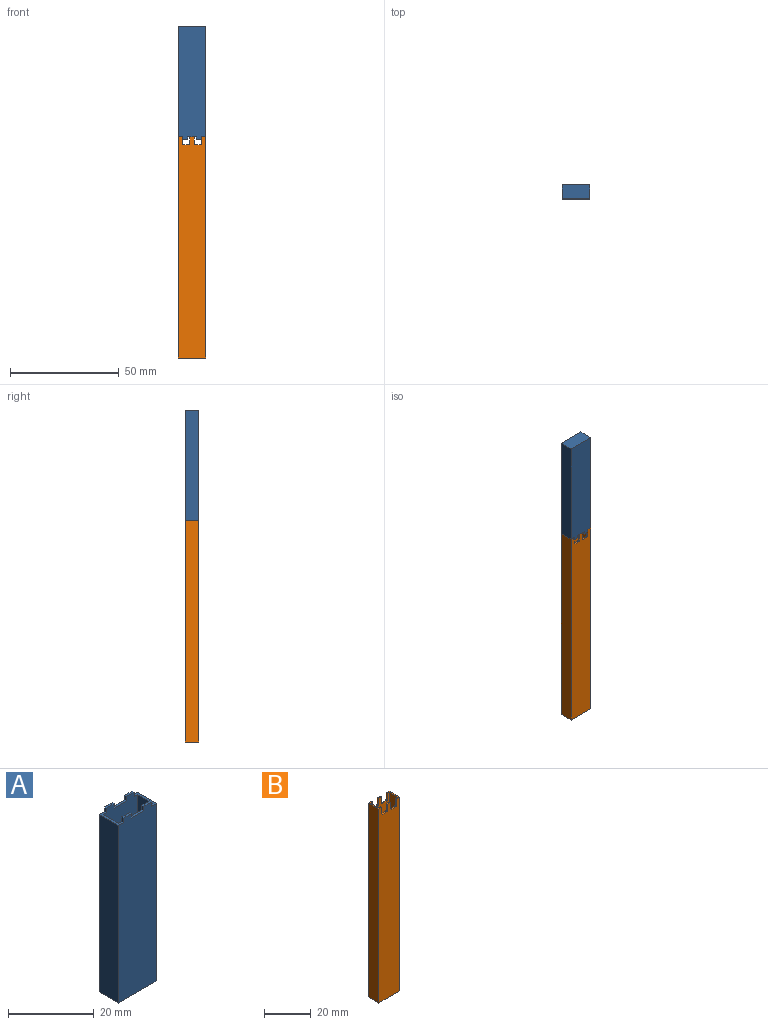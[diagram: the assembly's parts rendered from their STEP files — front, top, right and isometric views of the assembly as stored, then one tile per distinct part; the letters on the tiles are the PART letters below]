
ASSEMBLY  parts=2 mates=1
PART A: 26 faces, bbox 12.7x6.4x52.1 mm
  f0: plane 2.54x0.64mm, normal (0,0,1), area 1.6mm2, adj f9,f15,f20,f22
  f1: plane 2.54x0.64mm, normal (0,0,1), area 1.6mm2, adj f9,f15,f23,f24
  f2: plane 1.27x0.64mm, normal (1,0,0), area 0.8mm2, adj f7,f8,f13,f21
  f3: plane 1.27x0.64mm, normal (-1,0,0), area 0.8mm2, adj f8,f11,f13,f21
  f4: plane 1.27x0.64mm, normal (-1,0,0), area 0.8mm2, adj f7,f8,f13,f25
  f5: plane 1.27x0.64mm, normal (1,0,0), area 0.8mm2, adj f8,f10,f13,f25
  f6: plane 4.06x0.64mm, normal (0,0,1), area 2.6mm2, adj f9,f15,f20,f23
  f7: plane 4.06x0.64mm, normal (0,0,1), area 2.6mm2, adj f2,f4,f8,f13
  f8: plane 51.44x11.43mm, normal (0,-1,0), area 579.8mm2, adj f2,f3,f4,f5,f7,f10,f11,f17
  f9: plane 51.44x11.43mm, normal (0,1,0), area 579.8mm2, adj f0,f1,f6,f10,f11,f17,f18,f19
  f10: plane 6.35x1.78mm, normal (0,0,1), area 5.5mm2, adj f5,f8,f9,f12,f13,f15,f17,f24
  f11: plane 6.35x1.78mm, normal (0,0,1), area 5.5mm2, adj f3,f8,f9,f13,f14,f15,f18,f22
  f12: plane 50.8x6.35mm, normal (1,0,0), area 322.6mm2, adj f10,f13,f15,f16
  f13: plane 52.07x12.7mm, normal (0,1,0), area 651.6mm2, adj f2,f3,f4,f5,f7,f10,f11,f12
  f14: plane 50.8x6.35mm, normal (-1,0,0), area 322.6mm2, adj f11,f13,f15,f16
  f15: plane 52.07x12.7mm, normal (0,-1,0), area 651.6mm2, adj f0,f1,f6,f10,f11,f12,f14,f16
  f16: plane 12.7x6.35mm, normal (0,0,-1), area 80.6mm2, adj f12,f13,f14,f15
  f17: plane 50.17x5.08mm, normal (-1,0,0), area 254.8mm2, adj f8,f9,f10,f19
  f18: plane 50.17x5.08mm, normal (1,0,0), area 254.8mm2, adj f8,f9,f11,f19
  f19: plane 11.43x5.08mm, normal (0,0,1), area 58.1mm2, adj f8,f9,f17,f18
  f20: plane 1.27x0.64mm, normal (1,0,0), area 0.8mm2, adj f0,f6,f9,f15
  f21: plane 2.54x0.64mm, normal (0,0,1), area 1.6mm2, adj f2,f3,f8,f13
  f22: plane 1.27x0.64mm, normal (-1,0,0), area 0.8mm2, adj f0,f9,f11,f15
  f23: plane 1.27x0.64mm, normal (-1,0,0), area 0.8mm2, adj f1,f6,f9,f15
  f24: plane 1.27x0.64mm, normal (1,0,0), area 0.8mm2, adj f1,f9,f10,f15
  f25: plane 2.54x0.64mm, normal (0,0,1), area 1.6mm2, adj f4,f5,f8,f13
PART B: 34 faces, bbox 12.7x6.4x101.6 mm
  f0: plane 1.88x0.64mm, normal (0,0,1), area 1.2mm2, adj f5,f10,f24,f33
  f1: plane 1.88x0.64mm, normal (0,0,1), area 1.2mm2, adj f7,f12,f18,f19
  f2: plane 6.35x1.88mm, normal (0,0,1), area 5.6mm2, adj f4,f5,f7,f9,f10,f12,f14,f28
  f3: plane 6.35x1.88mm, normal (0,0,1), area 5.6mm2, adj f5,f6,f7,f10,f11,f12,f23,f29
  f4: plane 101.6x6.35mm, normal (1,0,0), area 645.2mm2, adj f2,f5,f7,f8
  f5: plane 101.6x12.7mm, normal (0,1,0), area 1263.8mm2, adj f0,f2,f3,f4,f6,f8,f24,f25
  f6: plane 101.6x6.35mm, normal (-1,0,0), area 645.2mm2, adj f3,f5,f7,f8
  f7: plane 101.6x12.7mm, normal (0,-1,0), area 1263.8mm2, adj f1,f2,f3,f4,f6,f8,f14,f15
  f8: plane 12.7x6.35mm, normal (0,0,-1), area 80.6mm2, adj f4,f5,f6,f7
  f9: plane 100.97x5.08mm, normal (-1,0,0), area 512.9mm2, adj f2,f10,f12,f13
  f10: plane 100.97x11.43mm, normal (0,-1,0), area 1127.5mm2, adj f0,f2,f3,f9,f11,f13,f24,f25
  f11: plane 100.97x5.08mm, normal (1,0,0), area 512.9mm2, adj f3,f10,f12,f13
  f12: plane 100.97x11.43mm, normal (0,1,0), area 1127.5mm2, adj f1,f2,f3,f9,f11,f13,f14,f15
  f13: plane 11.43x5.08mm, normal (0,0,1), area 58.1mm2, adj f9,f10,f11,f12
  f14: plane 3.18x0.64mm, normal (-1,0,0), area 2mm2, adj f2,f7,f12,f15
  f15: cylinder r=0.64mm len=0.64mm, axis (0,-1,0), area 0.6mm2, adj f7,f12,f14,f16
  f16: plane 2.26x0.64mm, normal (0,0,1), area 1.4mm2, adj f7,f12,f15,f17
  f17: cylinder r=0.64mm len=0.64mm, axis (0,-1,0), area 0.6mm2, adj f7,f12,f16,f18
  f18: plane 3.18x0.64mm, normal (1,0,0), area 2mm2, adj f1,f7,f12,f17
  f19: plane 3.18x0.64mm, normal (-1,0,0), area 2mm2, adj f1,f7,f12,f20
  f20: cylinder r=0.64mm len=0.64mm, axis (0,-1,0), area 0.6mm2, adj f7,f12,f19,f21
  f21: plane 2.26x0.64mm, normal (0,0,1), area 1.4mm2, adj f7,f12,f20,f22
  f22: cylinder r=0.64mm len=0.64mm, axis (0,-1,0), area 0.6mm2, adj f7,f12,f21,f23
  f23: plane 3.18x0.64mm, normal (1,0,0), area 2mm2, adj f3,f7,f12,f22
  f24: plane 3.18x0.64mm, normal (1,0,0), area 2mm2, adj f0,f5,f10,f25
  f25: cylinder r=0.64mm len=0.64mm, axis (0,-1,0), area 0.6mm2, adj f5,f10,f24,f26
  f26: plane 2.26x0.64mm, normal (0,0,1), area 1.4mm2, adj f5,f10,f25,f27
  f27: cylinder r=0.64mm len=0.64mm, axis (0,-1,0), area 0.6mm2, adj f5,f10,f26,f28
  f28: plane 3.18x0.64mm, normal (-1,0,0), area 2mm2, adj f2,f5,f10,f27
  f29: plane 3.18x0.64mm, normal (1,0,0), area 2mm2, adj f3,f5,f10,f30
  f30: cylinder r=0.64mm len=0.64mm, axis (0,-1,0), area 0.6mm2, adj f5,f10,f29,f31
  f31: plane 2.26x0.64mm, normal (0,0,1), area 1.4mm2, adj f5,f10,f30,f32
  f32: cylinder r=0.64mm len=0.64mm, axis (0,-1,0), area 0.6mm2, adj f5,f10,f31,f33
  f33: plane 3.18x0.64mm, normal (-1,0,0), area 2mm2, adj f0,f5,f10,f32
PLACE A rot(axis=(0,1,0),180deg) t=(0.35,-0.73,148.37)mm
PLACE B t=(0.35,-0.73,-4.03)mm
MATE fastened A.f11 <-> B.f2  axis (0,0,1) through (6.7,-0.73,97.57)mm
